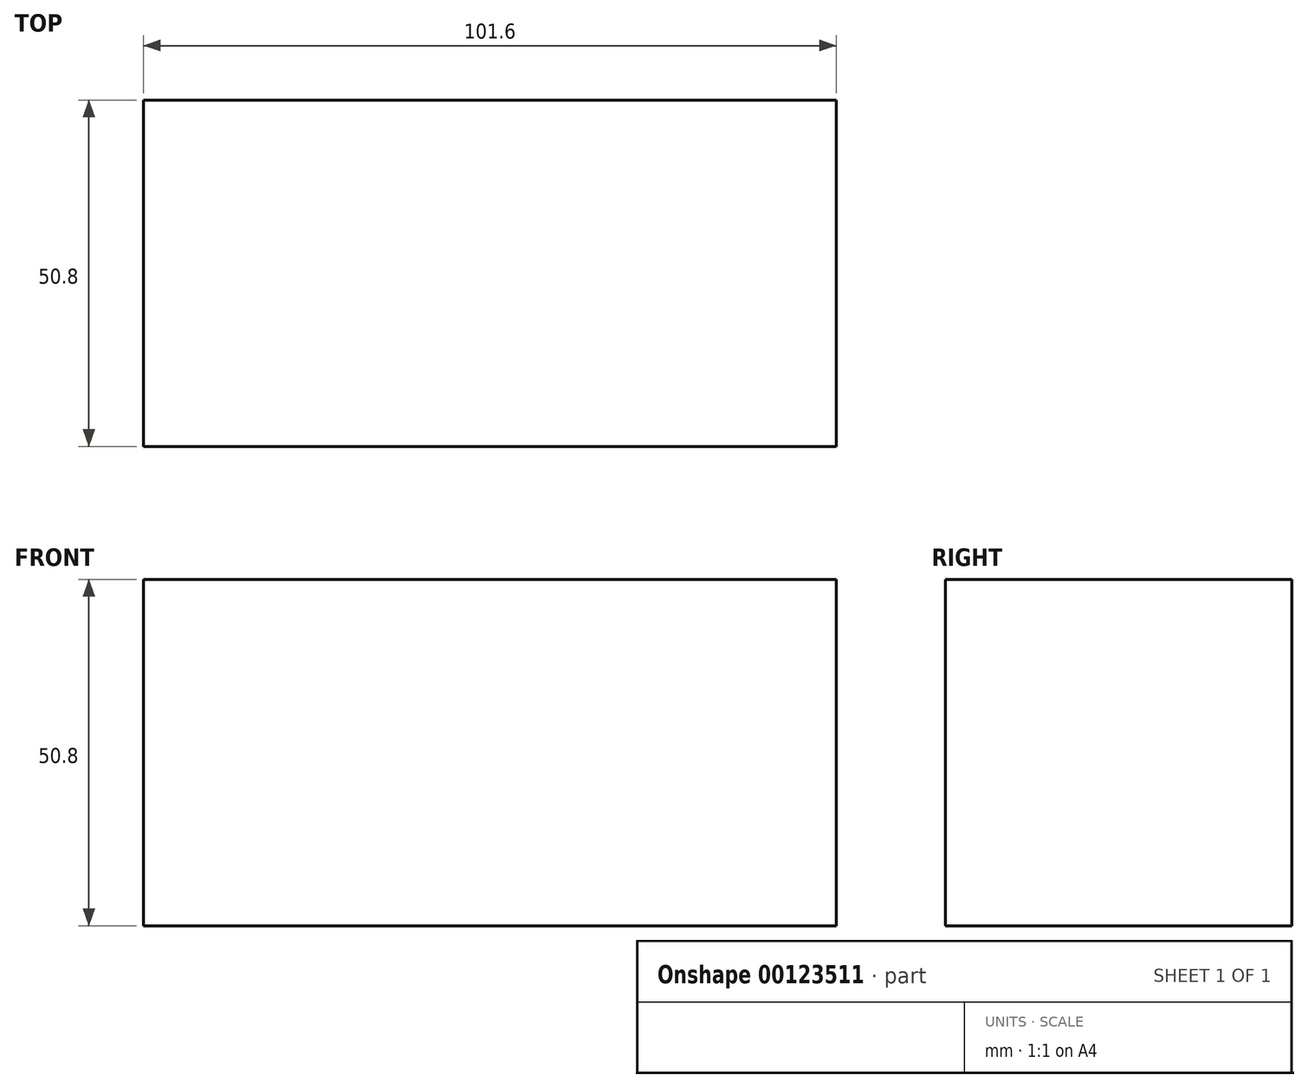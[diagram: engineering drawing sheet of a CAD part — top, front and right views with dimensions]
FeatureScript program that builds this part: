
annotation { "Feature Type Name" : "Feature", "Feature Type Description" : "" }
export const myFeature = defineFeature(function(context is Context, id is Id, definition is map)
    precondition{}
    {
        {
            var Q0;
            Q0=qCreatedBy(makeId("Front.planeOp"),FACE);
            var sketch = newSketch(context, id + "F0", { "sketchPlane" : qUnion([Q0])});
            skLineSegment(sketch, "E0.bottom", {"start": v(50.8, -25.4) * mm, "end": v(-50.8, -25.4) * mm});
            skLineSegment(sketch, "E0.top", {"start": v(50.8, 25.4) * mm, "end": v(-50.8, 25.4) * mm});
            skLineSegment(sketch, "E0.left", {"start": v(50.8, -25.4) * mm, "end": v(50.8, 25.4) * mm});
            skLineSegment(sketch, "E0.right", {"start": v(-50.8, -25.4) * mm, "end": v(-50.8, 25.4) * mm});
            skPoint(sketch, "E0.middle", {"position": v(0, 0) * mm});
            skSolve(sketch);
        }
        {
            var Q0;
            Q0 = qSketchRegion(id + "F0", true);
            extrude(context, id + "F1", {"entities" : qUnion([Q0]), "endBound" : BoundingType.SYMMETRIC, "depth" : 50.8 * mm});
        }
    });
